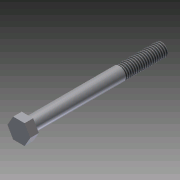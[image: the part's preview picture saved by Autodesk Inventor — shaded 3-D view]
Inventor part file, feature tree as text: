
AUTODESK INVENTOR PART (.ipt)
format: ipt  version: 2011 (Build 150239000, 239)  size: 78,848 bytes
history: native  units: in
note: dims shown in document units (in); Inventor stores cm internally (conversion verified against a paired STEP export)
features: extrude x2, sketch x2, thread x1
ambient origin geometry x8: Origin, YZ Plane, XZ Plane, XY Plane, X Axis, Y Axis, Z Axis, Center Point
bodies: Solid1 (feature_tree)
feature tree (5):
  extrude  "Extrusion1"  Depth=3.74in TaperAngle=0.0deg
  thread  "Thread1"  [1 undecoded]
  extrude  "Extrusion2"  Depth=0.239in TaperAngle=0.0deg
  sketch  "Sketch1"  dims[d0=0.367in d1=3.74in d2=0.0in d3=1.175in d4=0.0in]
  sketch  "Sketch2"  dims[d5=0.552in d6=0.239in d7=0.0in]
note: 1 required parameter value undecoded (feature->parameter linkage not recoverable at this tier; creation-order binding heuristic only, values carry confidence <= 0.55)
